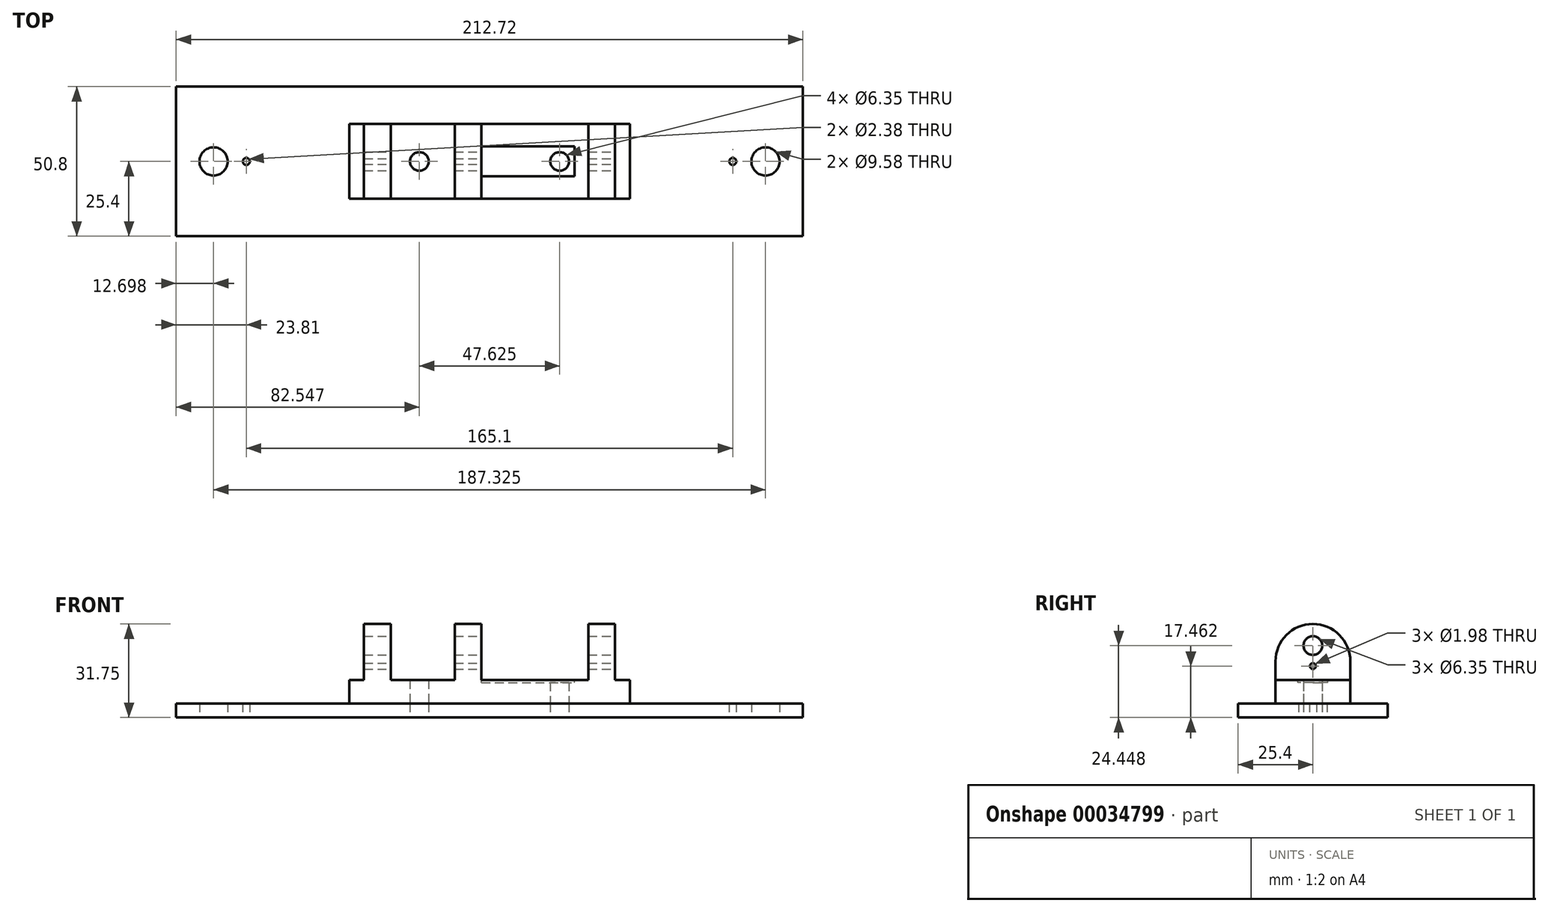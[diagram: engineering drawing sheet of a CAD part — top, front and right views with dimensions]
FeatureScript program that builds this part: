
annotation { "Feature Type Name" : "Feature", "Feature Type Description" : "" }
export const myFeature = defineFeature(function(context is Context, id is Id, definition is map)
    precondition{}
    {
        {
            var Q0;
            Q0=qCreatedBy(makeId("Top.planeOp"),FACE);
            var sketch = newSketch(context, id + "F0", { "sketchPlane" : qUnion([Q0])});
            skLineSegment(sketch, "E0.rect.bottom", {"start": v(106.36, 25.4) * mm, "end": v(-106.36, 25.4) * mm});
            skLineSegment(sketch, "E0.rect.top", {"start": v(106.36, -25.4) * mm, "end": v(-106.36, -25.4) * mm});
            skLineSegment(sketch, "E0.rect.left", {"start": v(106.36, 25.4) * mm, "end": v(106.36, -25.4) * mm});
            skLineSegment(sketch, "E0.rect.right", {"start": v(-106.36, 25.4) * mm, "end": v(-106.36, -25.4) * mm});
            skPoint(sketch, "E0.rect.middle", {"position": v(0, 0) * mm});
            skCircle(sketch, "E1", {"center": v(-93.66, 0) * mm, "radius": 4.79 * mm});
            skCircle(sketch, "E2", {"center": v(93.66, 0) * mm, "radius": 4.79 * mm});
            skLineSegment(sketch, "E3", {"start": v(-93.66, 0) * mm, "end": v(-106.36, 0) * mm, "construction": true});
            skLineSegment(sketch, "E4", {"start": v(93.66, 0) * mm, "end": v(106.36, 0) * mm, "construction": true});
            skCircle(sketch, "E5", {"center": v(-23.81, 0) * mm, "radius": 3.18 * mm});
            skCircle(sketch, "E6", {"center": v(23.81, 0) * mm, "radius": 3.18 * mm});
            skLineSegment(sketch, "E7", {"start": v(-23.81, 0) * mm, "end": v(0, 0) * mm, "construction": true});
            skLineSegment(sketch, "E8", {"start": v(23.81, 0) * mm, "end": v(0, 0) * mm, "construction": true});
            skCircle(sketch, "E9", {"center": v(-82.55, 0) * mm, "radius": 1.2 * mm});
            skCircle(sketch, "E10", {"center": v(82.55, 0) * mm, "radius": 1.2 * mm});
            skLineSegment(sketch, "E11", {"start": v(-93.66, 0) * mm, "end": v(-82.55, 0) * mm, "construction": true});
            skLineSegment(sketch, "E12", {"start": v(93.66, 0) * mm, "end": v(82.55, 0) * mm, "construction": true});
            skSolve(sketch);
        }
        {
            var Q0;
            Q0=makeQuery(id+"F0.imprint","IMPRINT",FACE,{"disambiguationData":[TD([[makeQuery(id+"F0.imprint","IMPRINT",EDGE,{"derivedFrom":sQuery(id+"F0.wireOp",EDGE,"E0.rect.bottom")}),1.0]])]});
            extrude(context, id + "F1", {"entities" : qUnion([Q0]), "depth" : 4.76 * mm});
        }
        {
            var Q0;
            Q0=qCreatedBy(makeId("Right.planeOp"),FACE);
            var sketch = newSketch(context, id + "F2", { "sketchPlane" : qUnion([Q0])});
            skLineSegment(sketch, "E13", {"start": v(-12.7, 4.76) * mm, "end": v(-12.7, 19.05) * mm});
            skArc(sketch, "E14", {"start": v(12.7, 19.05) * mm, "mid": v(0, 31.75) * mm, "end": v(-12.7, 19.05) * mm});
            skLineSegment(sketch, "E15", {"start": v(-12.7, 4.76) * mm, "end": v(12.7, 4.76) * mm});
            skLineSegment(sketch, "E16", {"start": v(12.7, 4.76) * mm, "end": v(12.7, 19.05) * mm});
            skLineSegment(sketch, "E17", {"start": v(0, 19.05) * mm, "end": v(0, 0) * mm, "construction": true});
            skSolve(sketch);
        }
        {
            var Q0;
            Q0 = qSketchRegion(id + "F2", true);
            extrude(context, id + "F3", {"entities" : qUnion([Q0]), "depth" : 47.62 * mm, "hasSecondDirection" : true, "secondDirectionOppositeDirection" : true, "secondDirectionDepth" : 47.62 * mm});
        }
        {
            var Q0;
            Q0=makeQuery(id+"F1.opExtrude","CAP_FACE",FACE,{"disambiguationData":[OSD([sQuery(id+"F0.wireOp",EDGE,"E0.rect.bottom"),sQuery(id+"F0.wireOp",EDGE,"E0.rect.top"),sQuery(id+"F0.wireOp",EDGE,"E0.rect.left"),sQuery(id+"F0.wireOp",EDGE,"E0.rect.right"),sQuery(id+"F0.wireOp",EDGE,"E1"),sQuery(id+"F0.wireOp",EDGE,"E2"),sQuery(id+"F0.wireOp",EDGE,"E5"),sQuery(id+"F0.wireOp",EDGE,"E6"),sQuery(id+"F0.wireOp",EDGE,"E9"),sQuery(id+"F0.wireOp",EDGE,"E10")])],"isStart":false});
            cPlane(context, id + "F4", {"entities" : qUnion([Q0]), "cplaneType" : CPlaneType.OFFSET, "offset" : 7.94 * mm, "width" : 152.4 * mm, "height" : 152.4 * mm});
        }
        {
            var Q0;
            Q0=qCreatedBy(id+"F4.planeOp",FACE);
            var sketch = newSketch(context, id + "F5", { "sketchPlane" : qUnion([Q0])});
            skLineSegment(sketch, "E18.bottom", {"start": v(-47.63, 12.7) * mm, "end": v(-42.6, 12.7) * mm});
            skLineSegment(sketch, "E18.top", {"start": v(-47.63, -12.7) * mm, "end": v(-42.6, -12.7) * mm});
            skLineSegment(sketch, "E18.left", {"start": v(-47.63, 12.7) * mm, "end": v(-47.63, -12.7) * mm});
            skLineSegment(sketch, "E18.right", {"start": v(-42.6, 12.7) * mm, "end": v(-42.6, -12.7) * mm});
            skLineSegment(sketch, "E19.bottom", {"start": v(-33.54, 12.7) * mm, "end": v(-11.85, 12.7) * mm});
            skLineSegment(sketch, "E19.top", {"start": v(-33.54, -12.7) * mm, "end": v(-11.85, -12.7) * mm});
            skLineSegment(sketch, "E19.left", {"start": v(-33.54, 12.7) * mm, "end": v(-33.54, -12.7) * mm});
            skLineSegment(sketch, "E19.right", {"start": v(-11.85, 12.7) * mm, "end": v(-11.85, -12.7) * mm});
            skLineSegment(sketch, "E20.bottom", {"start": v(-2.78, 12.7) * mm, "end": v(33.54, 12.7) * mm});
            skLineSegment(sketch, "E20.top", {"start": v(-2.78, -12.7) * mm, "end": v(33.54, -12.7) * mm});
            skLineSegment(sketch, "E20.left", {"start": v(-2.78, 12.7) * mm, "end": v(-2.78, -12.7) * mm});
            skLineSegment(sketch, "E20.right", {"start": v(33.54, 12.7) * mm, "end": v(33.54, -12.7) * mm});
            skLineSegment(sketch, "E21.bottom", {"start": v(42.6, 12.7) * mm, "end": v(47.63, 12.7) * mm});
            skLineSegment(sketch, "E21.top", {"start": v(42.6, -12.7) * mm, "end": v(47.63, -12.7) * mm});
            skLineSegment(sketch, "E21.left", {"start": v(42.6, 12.7) * mm, "end": v(42.6, -12.7) * mm});
            skLineSegment(sketch, "E21.right", {"start": v(47.63, 12.7) * mm, "end": v(47.63, -12.7) * mm});
            skLineSegment(sketch, "E22", {"start": v(-33.54, 0) * mm, "end": v(-42.6, 0) * mm, "construction": true});
            skLineSegment(sketch, "E23", {"start": v(-2.78, 0) * mm, "end": v(-11.85, 0) * mm, "construction": true});
            skLineSegment(sketch, "E24", {"start": v(42.6, 0) * mm, "end": v(33.54, 0) * mm, "construction": true});
            skLineSegment(sketch, "E25", {"start": v(-42.6, 0) * mm, "end": v(-47.63, 0) * mm, "construction": true});
            skLineSegment(sketch, "E26", {"start": v(42.6, 0) * mm, "end": v(47.63, 0) * mm, "construction": true});
            skSolve(sketch);
        }
        {
            var Q0;
            Q0 = qSketchRegion(id + "F5", true);
            extrude(context, id + "F6", {"entities" : qUnion([Q0]), "operationType" : NewBodyOperationType.REMOVE, "depth" : 25.4 * mm});
        }
        {
            var Q0;
            Q0=makeQuery(id+"F3.opExtrude","SWEPT_FACE",FACE,{"disambiguationData":[OSD([sQuery(id+"F2.wireOp",EDGE,"E15")])]});
            var sketch = newSketch(context, id + "F7", { "sketchPlane" : qUnion([Q0])});
            skCircle(sketch, "E27.0", {"center": v(-23.81, 0) * mm, "radius": 3.18 * mm});
            skCircle(sketch, "E27.1", {"center": v(23.81, 0) * mm, "radius": 3.18 * mm});
            skSolve(sketch);
        }
        {
            var Q0;
            Q0 = qSketchRegion(id + "F7", true);
            extrude(context, id + "F8", {"entities" : qUnion([Q0]), "operationType" : NewBodyOperationType.REMOVE, "oppositeDirection" : true, "depth" : 25.4 * mm});
        }
        {
            var Q0;
            Q0=makeQuery(id+"F6.boolean.opBoolean","COPY",FACE,{"derivedFrom":makeQuery(id+"F6.opExtrude","CAP_FACE",FACE,{"disambiguationData":[OSD([sQuery(id+"F5.wireOp",EDGE,"E20.bottom"),sQuery(id+"F5.wireOp",EDGE,"E20.top"),sQuery(id+"F5.wireOp",EDGE,"E20.left"),sQuery(id+"F5.wireOp",EDGE,"E20.right")])],"isStart":true})});
            var sketch = newSketch(context, id + "F9", { "sketchPlane" : qUnion([Q0])});
            skLineSegment(sketch, "E28.bottom", {"start": v(-2.78, -5.08) * mm, "end": v(28.9, -5.08) * mm});
            skLineSegment(sketch, "E28.top", {"start": v(-2.78, 5.08) * mm, "end": v(28.9, 5.08) * mm});
            skLineSegment(sketch, "E28.left", {"start": v(-2.78, -5.08) * mm, "end": v(-2.78, 5.08) * mm});
            skLineSegment(sketch, "E28.right", {"start": v(28.9, -5.08) * mm, "end": v(28.9, 5.08) * mm});
            skLineSegment(sketch, "E29", {"start": v(23.81, 0) * mm, "end": v(23.81, 5.08) * mm, "construction": true});
            skLineSegment(sketch, "E30", {"start": v(23.81, 0) * mm, "end": v(28.9, 0) * mm, "construction": true});
            skLineSegment(sketch, "E31", {"start": v(23.81, 0) * mm, "end": v(23.81, -5.08) * mm, "construction": true});
            skSolve(sketch);
        }
        {
            var Q0;
            Q0 = qSketchRegion(id + "F9", true);
            extrude(context, id + "F10", {"entities" : qUnion([Q0]), "operationType" : NewBodyOperationType.REMOVE, "oppositeDirection" : true, "depth" : 0.8 * mm});
        }
        {
            var Q0;
            Q0=makeQuery(id+"F6.boolean.opBoolean","COPY",FACE,{"derivedFrom":makeQuery(id+"F6.opExtrude","SWEPT_FACE",FACE,{"disambiguationData":[OSD([sQuery(id+"F5.wireOp",EDGE,"E21.left")])]})});
            var sketch = newSketch(context, id + "F11", { "sketchPlane" : qUnion([Q0])});
            skCircle(sketch, "E32", {"center": v(0, 24.45) * mm, "radius": 3.18 * mm});
            skCircle(sketch, "E33", {"center": v(0, 17.46) * mm, "radius": 1 * mm});
            skSolve(sketch);
        }
        {
            var Q0;
            Q0 = qSketchRegion(id + "F11", true);
            extrude(context, id + "F12", {"entities" : qUnion([Q0]), "operationType" : NewBodyOperationType.REMOVE, "endBound" : BoundingType.THROUGH_ALL, "oppositeDirection" : true, "depth" : 25.4 * mm});
        }
    });
